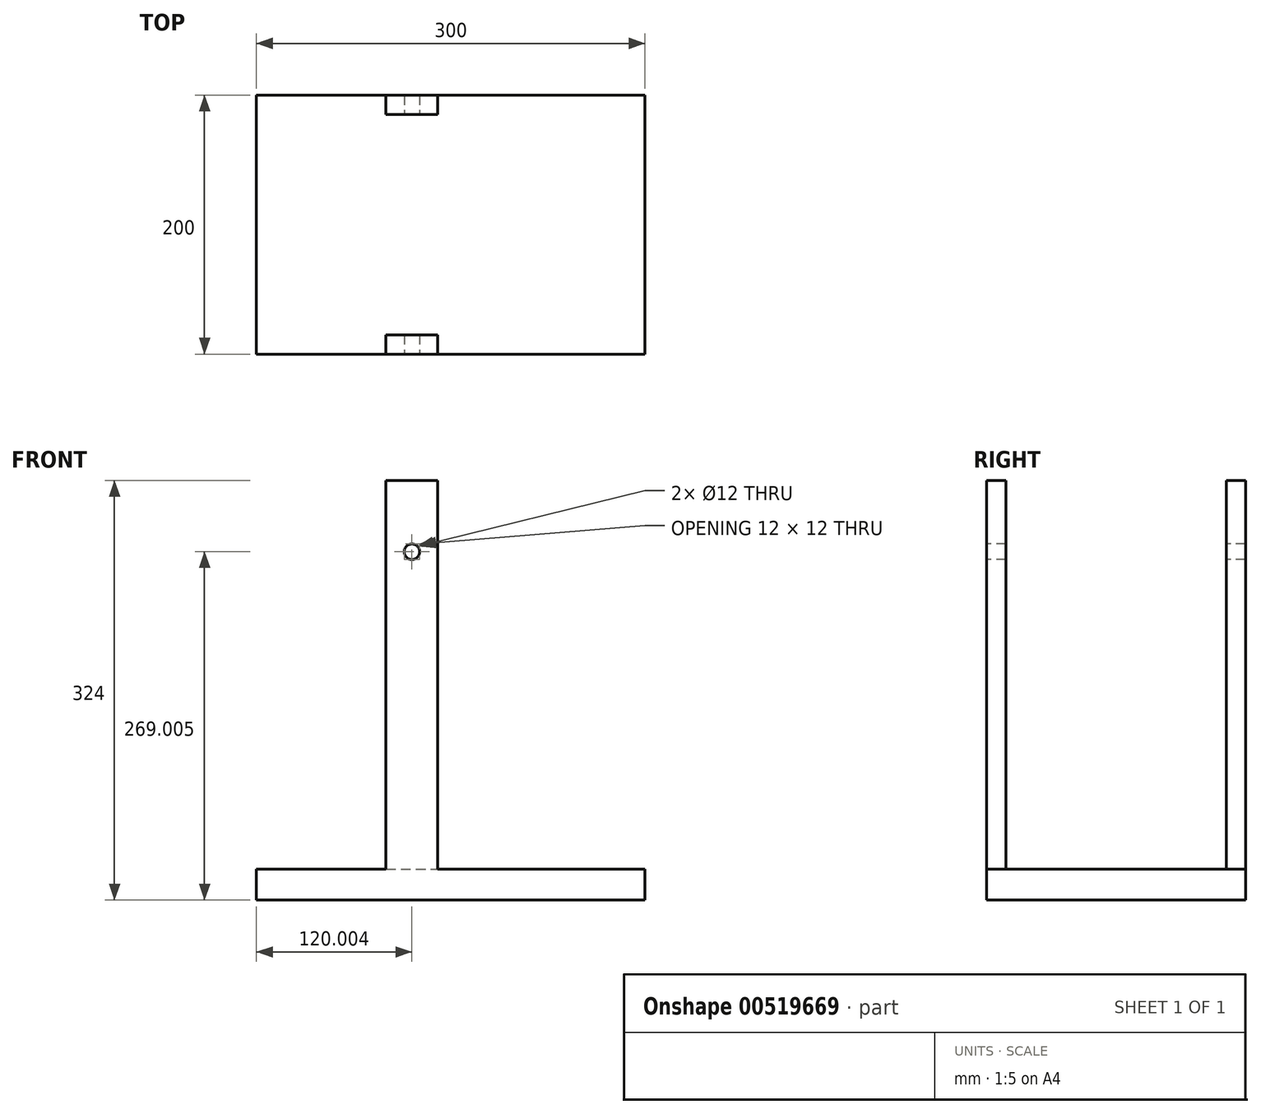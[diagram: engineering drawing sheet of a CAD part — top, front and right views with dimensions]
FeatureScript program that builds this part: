
annotation { "Feature Type Name" : "Feature", "Feature Type Description" : "" }
export const myFeature = defineFeature(function(context is Context, id is Id, definition is map)
    precondition{}
    {
        {
            var Q0;
            Q0=qCreatedBy(makeId("Front.planeOp"),FACE);
            var sketch = newSketch(context, id + "F0", { "sketchPlane" : qUnion([Q0])});
            skLineSegment(sketch, "E0.bottom", {"start": v(-155.2, -8.06) * mm, "end": v(144.8, -8.06) * mm});
            skLineSegment(sketch, "E0.top", {"start": v(-155.2, -32.06) * mm, "end": v(144.8, -32.06) * mm});
            skLineSegment(sketch, "E0.left", {"start": v(-155.2, -8.06) * mm, "end": v(-155.2, -32.06) * mm});
            skLineSegment(sketch, "E0.right", {"start": v(144.8, -8.06) * mm, "end": v(144.8, -32.06) * mm});
            skSolve(sketch);
        }
        {
            var Q0;
            Q0=makeQuery(id+"F0.imprint","IMPRINT",FACE,{"disambiguationData":[TD([[makeQuery(id+"F0.imprint","IMPRINT",EDGE,{"derivedFrom":sQuery(id+"F0.wireOp",EDGE,"E0.bottom")}),-1.0]])]});
            extrude(context, id + "F1", {"entities" : qUnion([Q0]), "endBound" : BoundingType.SYMMETRIC, "depth" : 200 * mm, "offsetDistance" : 25 * mm});
        }
        {
            var Q0;
            Q0=makeQuery(id+"F1.opExtrude","SWEPT_FACE",FACE,{"disambiguationData":[OSD([sQuery(id+"F0.wireOp",EDGE,"E0.bottom")])]});
            var sketch = newSketch(context, id + "F2", { "sketchPlane" : qUnion([Q0])});
            skLineSegment(sketch, "E1.bottom", {"start": v(-55.2, -85) * mm, "end": v(-15.2, -85) * mm});
            skLineSegment(sketch, "E1.top", {"start": v(-55.2, -100) * mm, "end": v(-15.2, -100) * mm});
            skLineSegment(sketch, "E1.left", {"start": v(-55.2, -85) * mm, "end": v(-55.2, -100) * mm});
            skLineSegment(sketch, "E1.right", {"start": v(-15.2, -85) * mm, "end": v(-15.2, -100) * mm});
            skLineSegment(sketch, "E2.bottom", {"start": v(-55.2, 100) * mm, "end": v(-15.2, 100) * mm});
            skLineSegment(sketch, "E2.top", {"start": v(-55.2, 85) * mm, "end": v(-15.2, 85) * mm});
            skLineSegment(sketch, "E2.left", {"start": v(-55.2, 100) * mm, "end": v(-55.2, 85) * mm});
            skLineSegment(sketch, "E2.right", {"start": v(-15.2, 100) * mm, "end": v(-15.2, 85) * mm});
            skSolve(sketch);
        }
        {
            var Q0;
            Q0 = qSketchRegion(id + "F2", true);
            extrude(context, id + "F3", {"entities" : qUnion([Q0]), "operationType" : NewBodyOperationType.ADD, "depth" : 300 * mm, "offsetDistance" : 25 * mm});
        }
        {
            var Q0;
            Q0=makeQuery(id+"F3.boolean.opBoolean","MERGE",FACE,{"derivedFrom":[makeQuery(id+"F1.opExtrude","CAP_FACE",FACE,{"disambiguationData":[OSD([sQuery(id+"F0.wireOp",EDGE,"E0.bottom"),sQuery(id+"F0.wireOp",EDGE,"E0.top"),sQuery(id+"F0.wireOp",EDGE,"E0.left"),sQuery(id+"F0.wireOp",EDGE,"E0.right")])],"isStart":false}),makeQuery(id+"F3.opExtrude","SWEPT_FACE",FACE,{"disambiguationData":[OSD([sQuery(id+"F2.wireOp",EDGE,"E1.top")])]})]});
            var sketch = newSketch(context, id + "F4", { "sketchPlane" : qUnion([Q0])});
            skCircle(sketch, "E3", {"center": v(-35.2, 236.94) * mm, "radius": 6 * mm});
            skSolve(sketch);
        }
        {
            var Q0;
            Q0=sQuery(id+"F4.wireOp",VERTEX,"E3.center");
            var Q1;
            Q1=makeQuery(id+"F1.opExtrude","SWEPT_BODY",BODY,{"disambiguationData":[OSD([sQuery(id+"F0.wireOp",EDGE,"E0.bottom"),sQuery(id+"F0.wireOp",EDGE,"E0.top"),sQuery(id+"F0.wireOp",EDGE,"E0.left"),sQuery(id+"F0.wireOp",EDGE,"E0.right")])]});
            hole(context, id + "F5", {"style" : HoleStyle.SIMPLE, "endStyle" : HoleEndStyle.THROUGH, "holeDiameter" : 12 * mm, "isTappedThrough" : true, "tappedDepth" : 12 * mm, "tapClearance" : 3, "locations" : qUnion([Q0]), "scope" : qUnion([Q1])});
        }
    });
